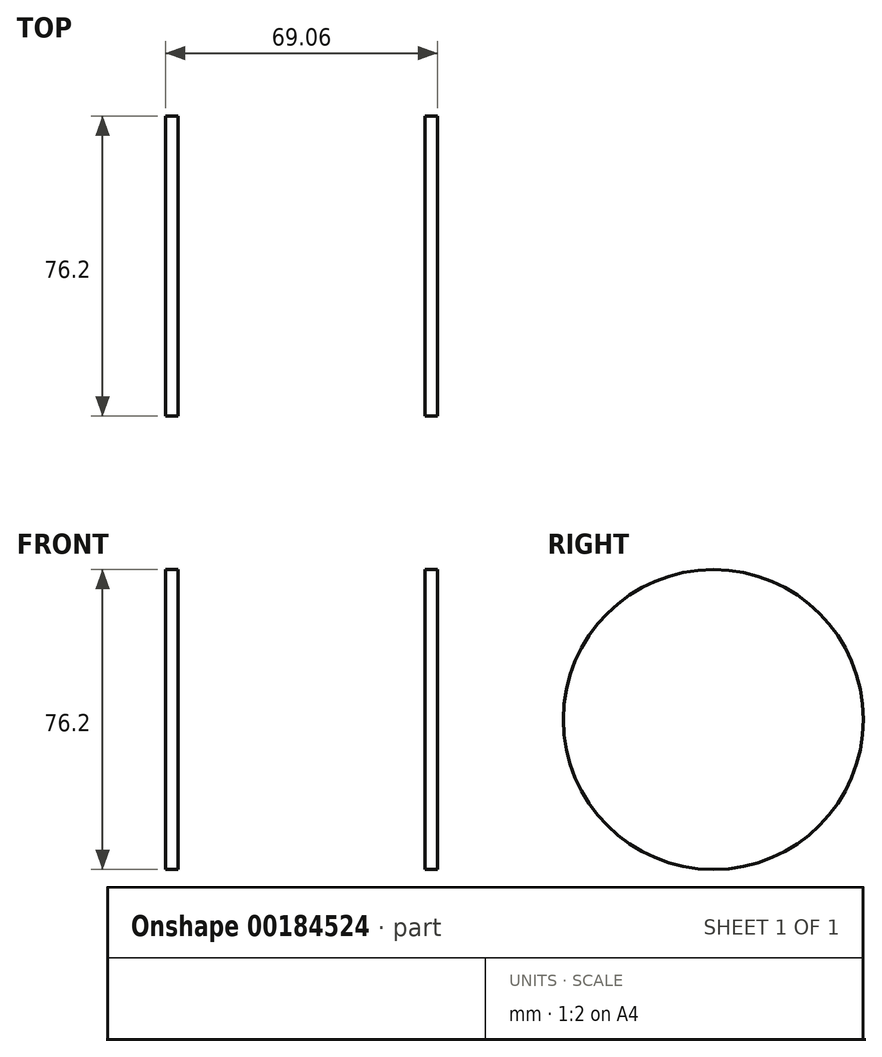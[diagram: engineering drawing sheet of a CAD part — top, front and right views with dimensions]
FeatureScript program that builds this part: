
annotation { "Feature Type Name" : "Feature", "Feature Type Description" : "" }
export const myFeature = defineFeature(function(context is Context, id is Id, definition is map)
    precondition{}
    {
        {
            var Q0;
            Q0=qCreatedBy(makeId("Front.planeOp"),FACE);
            var sketch = newSketch(context, id + "F0", { "sketchPlane" : qUnion([Q0])});
            skLineSegment(sketch, "E0", {"start": v(-31.35, 0) * mm, "end": v(-31.35, 38.1) * mm});
            skLineSegment(sketch, "E1", {"start": v(31.35, 0) * mm, "end": v(31.35, 38.1) * mm});
            skLineSegment(sketch, "E2", {"start": v(-31.35, 25.4) * mm, "end": v(31.35, 25.4) * mm});
            skLineSegment(sketch, "E3", {"start": v(-75.59, 0) * mm, "end": v(76.16, 0) * mm});
            skLineSegment(sketch, "E4.0", {"start": v(-34.53, 0) * mm, "end": v(-34.53, 38.1) * mm});
            skLineSegment(sketch, "E5.0", {"start": v(34.53, 0) * mm, "end": v(34.53, 38.1) * mm});
            skLineSegment(sketch, "E6", {"start": v(-34.53, 38.1) * mm, "end": v(-31.35, 38.1) * mm});
            skLineSegment(sketch, "E7", {"start": v(31.35, 38.1) * mm, "end": v(34.53, 38.1) * mm});
            skSolve(sketch);
        }
        {
            var Q0;
            {var subQ3=sQuery(id+"F0.wireOp",EDGE,"E2");Q0=makeQuery(id+"F0.imprint","IMPRINT",FACE,{"disambiguationData":[TD([[makeQuery(id+"F0.imprint","IMPRINT",EDGE,{"derivedFrom":subQ3}),-1.0]])]});}
            var Q1;
            Q1=sQuery(id+"F0.wireOp",EDGE,"E2");
            var Q2;
            Q2=sQuery(id+"F0.wireOp",EDGE,"E3");
            revolve(context, id + "F1", {"bodyType" : ToolBodyType.SURFACE, "operationType" : NewBodyOperationType.REMOVE, "entities" : qUnion([Q0]), "surfaceEntities" : qUnion([Q1]), "axis" : qUnion([Q2]), "revolveType" : RevolveType.FULL, "oppositeDirection" : true});
        }
        {
            var Q0;
            {var subQ0=sQuery(id+"F0.wireOp",EDGE,"E5.0");Q0=makeQuery(id+"F0.imprint","IMPRINT",FACE,{"disambiguationData":[TD([[makeQuery(id+"F0.imprint","IMPRINT",EDGE,{"derivedFrom":subQ0}),1.0]])]});}
            var Q1;
            Q1=sQuery(id+"F0.wireOp",EDGE,"E3");
            revolve(context, id + "F2", {"entities" : qUnion([Q0]), "axis" : qUnion([Q1]), "revolveType" : RevolveType.FULL});
        }
        {
            var Q0;
            {var subQ0=sQuery(id+"F0.wireOp",EDGE,"E4.0");Q0=makeQuery(id+"F0.imprint","IMPRINT",FACE,{"disambiguationData":[TD([[makeQuery(id+"F0.imprint","IMPRINT",EDGE,{"derivedFrom":subQ0}),-1.0]])]});}
            var Q1;
            Q1=makeQuery(id+"F1.opRevolve","SWEPT_FACE",FACE,{"disambiguationData":[OSD([sQuery(id+"F0.wireOp",EDGE,"E2")])]});
            revolve(context, id + "F3", {"entities" : qUnion([Q0]), "axis" : qUnion([Q1]), "revolveType" : RevolveType.FULL});
        }
    });
